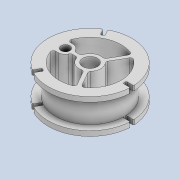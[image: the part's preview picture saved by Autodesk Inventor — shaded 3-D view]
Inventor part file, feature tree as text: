
AUTODESK INVENTOR PART (.ipt)
format: ipt  version: 2020 (Build 240168000, 168)  size: 404,992 bytes
history: native  units: mm
features: extrude x6, sketch x6, fillet x4, projected_geometry x4, pattern_circular x1, thicken_offset x1
ambient origin geometry x8: Origin, YZ Plane, XZ Plane, XY Plane, X Axis, Y Axis, Z Axis, Center Point
bodies: Solid1 (feature_tree)
feature tree (22):
  extrude  "Extrusion1"  Depth=3.0mm
  extrude  "Extrusion2"  Depth=0.7mm
  extrude  "Extrusion3"  Depth=0.7mm
  extrude  "Extrusion4"  Depth=5.0mm
  extrude  "Extrusion5"  Depth=7.0mm TaperAngle=0.0deg
  pattern_circular  "Circular Pattern1"  [2 undecoded]
  fillet  "Fillet1"  Radius=1.5mm
  fillet  "Fillet2"  Radius=1.0mm
  extrude  "Extrusion6"  Depth=0.5mm TaperAngle=0.0deg
  fillet  "Fillet3"  [1 undecoded]
  fillet  "Fillet4"  Radius=3.0mm
  thicken_offset  "Thicken1"
  sketch  "Sketch1"  dims[d0=14.0mm d1=3.0mm]
  sketch  "Sketch2"  dims[d2=0.7mm d3=0.7mm]
  projected_geometry  "Projected Loop1"
  sketch  "Sketch3"  dims[d4=3.5mm d5=0.7mm]
  projected_geometry  "Projected Loop2"
  sketch  "Sketch4"  dims[d6=30.0mm d8=360.0deg d10=5.0mm]
  projected_geometry  "Projected Loop3"
  sketch  "Sketch5"  dims[d11=3.0mm d12=7.0mm d13=0.0mm]
  projected_geometry  "Projected Loop4"
  sketch  "Sketch6"  dims[d14=1.8mm d15=19.5mm d16=0.0mm d17=1.5mm d18=1.0mm d19=0.0mm d20=1.0mm d21=0.0mm d22=60.0deg d23=3.0mm d24=0.7mm d25=20.0mm d26=0.0mm d27=30.0mm d28=360.0deg d30=0.2mm d31=0.5mm d32=5.5mm d33=3.0mm d34=0.0mm d35=0.5mm d36=0.5mm d37=0.3mm d38=0.3mm]
note: 3 required parameter values undecoded (feature->parameter linkage not recoverable at this tier; creation-order binding heuristic only, values carry confidence <= 0.55)
